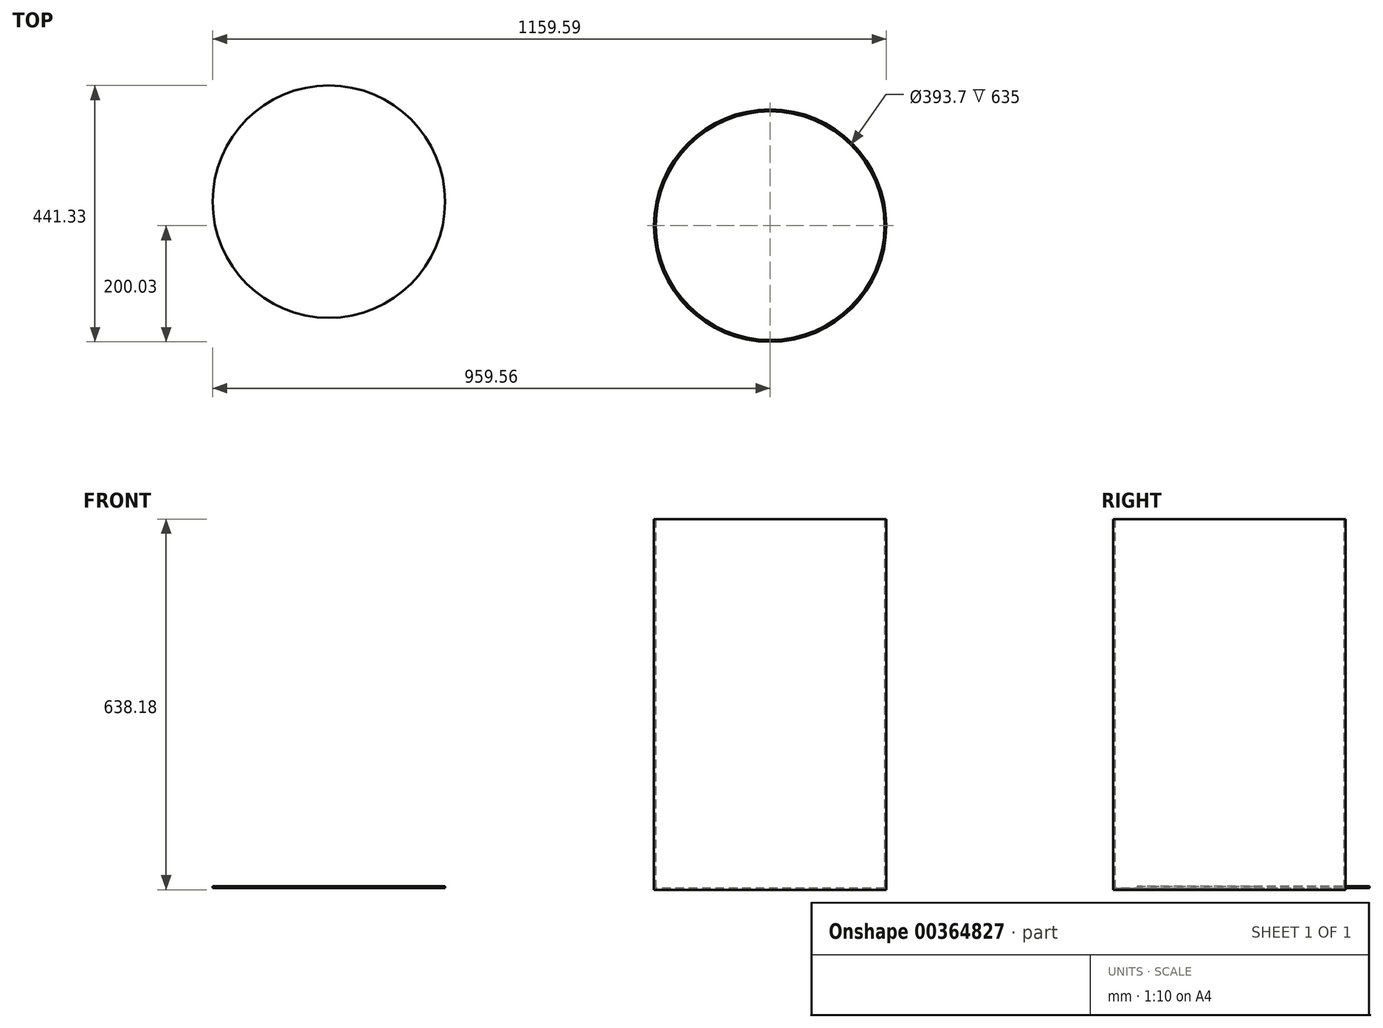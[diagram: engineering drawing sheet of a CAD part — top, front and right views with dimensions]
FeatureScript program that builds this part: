
annotation { "Feature Type Name" : "Feature", "Feature Type Description" : "" }
export const myFeature = defineFeature(function(context is Context, id is Id, definition is map)
    precondition{}
    {
        {
            var Q0;
            Q0=qCreatedBy(makeId("Top.planeOp"),FACE);
            var sketch = newSketch(context, id + "F0", { "sketchPlane" : qUnion([Q0])});
            skCircle(sketch, "E0", {"center": v(0, 0) * mm, "radius": 200.03 * mm});
            skSolve(sketch);
        }
        {
            var Q0;
            Q0=makeQuery(id+"F0.imprint","IMPRINT",FACE,{"disambiguationData":[TD([[makeQuery(id+"F0.imprint","IMPRINT",EDGE,{"derivedFrom":sQuery(id+"F0.wireOp",EDGE,"E0")}),1.0]])]});
            extrude(context, id + "F1", {"entities" : qUnion([Q0]), "oppositeDirection" : true, "depth" : 3.17 * mm, "offsetDistance" : 25.4 * mm});
        }
        {
            var Q0;
            Q0=makeQuery(id+"F1.opExtrude","CAP_FACE",FACE,{"disambiguationData":[OSD([sQuery(id+"F0.wireOp",EDGE,"E0")])],"isStart":true});
            var sketch = newSketch(context, id + "F2", { "sketchPlane" : qUnion([Q0])});
            skCircle(sketch, "E1", {"center": v(0, 0) * mm, "radius": 196.85 * mm});
            skSolve(sketch);
        }
        {
            var Q0;
            Q0=makeQuery(id+"F2.imprint","IMPRINT",FACE,{"disambiguationData":[TD([[makeQuery(id+"F2.imprint","IMPRINT",EDGE,{"derivedFrom":sQuery(id+"F2.wireOp",EDGE,"E1")}),-1.0]])]});
            extrude(context, id + "F3", {"entities" : qUnion([Q0]), "operationType" : NewBodyOperationType.ADD, "depth" : 635 * mm, "offsetDistance" : 25.4 * mm});
        }
        {
            var Q0;
            Q0=qCreatedBy(makeId("Top.planeOp"),FACE);
            var sketch = newSketch(context, id + "F4", { "sketchPlane" : qUnion([Q0])});
            skCircle(sketch, "E2", {"center": v(-759.54, 41.28) * mm, "radius": 200.03 * mm});
            skSolve(sketch);
        }
        {
            var Q0;
            Q0=makeQuery(id+"F4.imprint","IMPRINT",FACE,{"disambiguationData":[TD([[makeQuery(id+"F4.imprint","IMPRINT",EDGE,{"derivedFrom":sQuery(id+"F4.wireOp",EDGE,"E2")}),1.0]])]});
            extrude(context, id + "F5", {"entities" : qUnion([Q0]), "depth" : 3.17 * mm});
        }
    });
